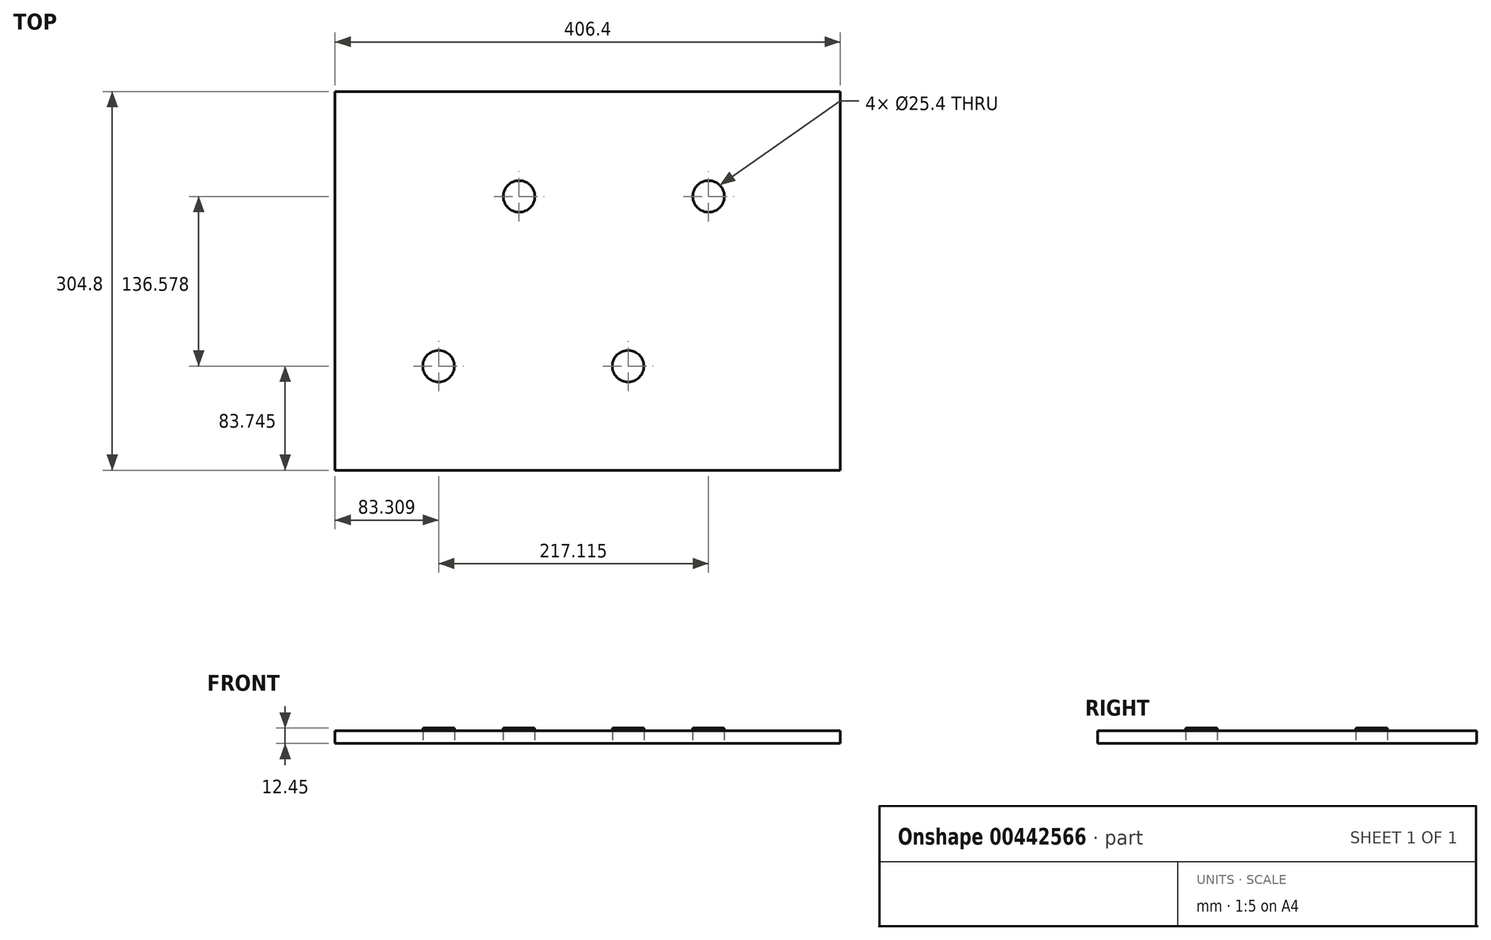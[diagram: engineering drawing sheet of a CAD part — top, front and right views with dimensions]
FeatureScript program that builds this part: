
annotation { "Feature Type Name" : "Feature", "Feature Type Description" : "" }
export const myFeature = defineFeature(function(context is Context, id is Id, definition is map)
    precondition{}
    {
        {
            var Q0;
            Q0=qCreatedBy(makeId("Top.planeOp"),FACE);
            var sketch = newSketch(context, id + "F0", { "sketchPlane" : qUnion([Q0])});
            skLineSegment(sketch, "E0.bottom", {"start": v(-140.6, 160.85) * mm, "end": v(265.8, 160.85) * mm});
            skLineSegment(sketch, "E0.top", {"start": v(-140.6, -143.95) * mm, "end": v(265.8, -143.95) * mm});
            skLineSegment(sketch, "E0.left", {"start": v(-140.6, 160.85) * mm, "end": v(-140.6, -143.95) * mm});
            skLineSegment(sketch, "E0.right", {"start": v(265.8, 160.85) * mm, "end": v(265.8, -143.95) * mm});
            skCircle(sketch, "E1", {"center": v(7.42, 76.37) * mm, "radius": 12.7 * mm});
            skCircle(sketch, "E2", {"center": v(159.82, 76.37) * mm, "radius": 12.7 * mm});
            skCircle(sketch, "E3", {"center": v(-57.3, -60.2) * mm, "radius": 12.7 * mm});
            skCircle(sketch, "E4", {"center": v(95.1, -60.2) * mm, "radius": 12.7 * mm});
            skSolve(sketch);
        }
        {
            var Q0;
            Q0=makeQuery(id+"F0.imprint","IMPRINT",FACE,{"disambiguationData":[TD([[makeQuery(id+"F0.imprint","IMPRINT",EDGE,{"derivedFrom":sQuery(id+"F0.wireOp",EDGE,"E1")}),1.0]])]});
            var Q1;
            Q1=makeQuery(id+"F0.imprint","IMPRINT",FACE,{"disambiguationData":[TD([[makeQuery(id+"F0.imprint","IMPRINT",EDGE,{"derivedFrom":sQuery(id+"F0.wireOp",EDGE,"E2")}),1.0]])]});
            var Q2;
            Q2=makeQuery(id+"F0.imprint","IMPRINT",FACE,{"disambiguationData":[TD([[makeQuery(id+"F0.imprint","IMPRINT",EDGE,{"derivedFrom":sQuery(id+"F0.wireOp",EDGE,"E3")}),1.0]])]});
            var Q3;
            Q3=makeQuery(id+"F0.imprint","IMPRINT",FACE,{"disambiguationData":[TD([[makeQuery(id+"F0.imprint","IMPRINT",EDGE,{"derivedFrom":sQuery(id+"F0.wireOp",EDGE,"E4")}),1.0]])]});
            extrude(context, id + "F1", {"entities" : qUnion([Q0, Q1, Q2, Q3]), "depth" : 12.45 * mm});
        }
        {
            var Q0;
            Q0=makeQuery(id+"F0.imprint","IMPRINT",FACE,{"disambiguationData":[TD([[makeQuery(id+"F0.imprint","IMPRINT",EDGE,{"derivedFrom":sQuery(id+"F0.wireOp",EDGE,"E0.bottom")}),-1.0]])]});
            extrude(context, id + "F2", {"entities" : qUnion([Q0]), "depth" : 10.16 * mm});
        }
    });
